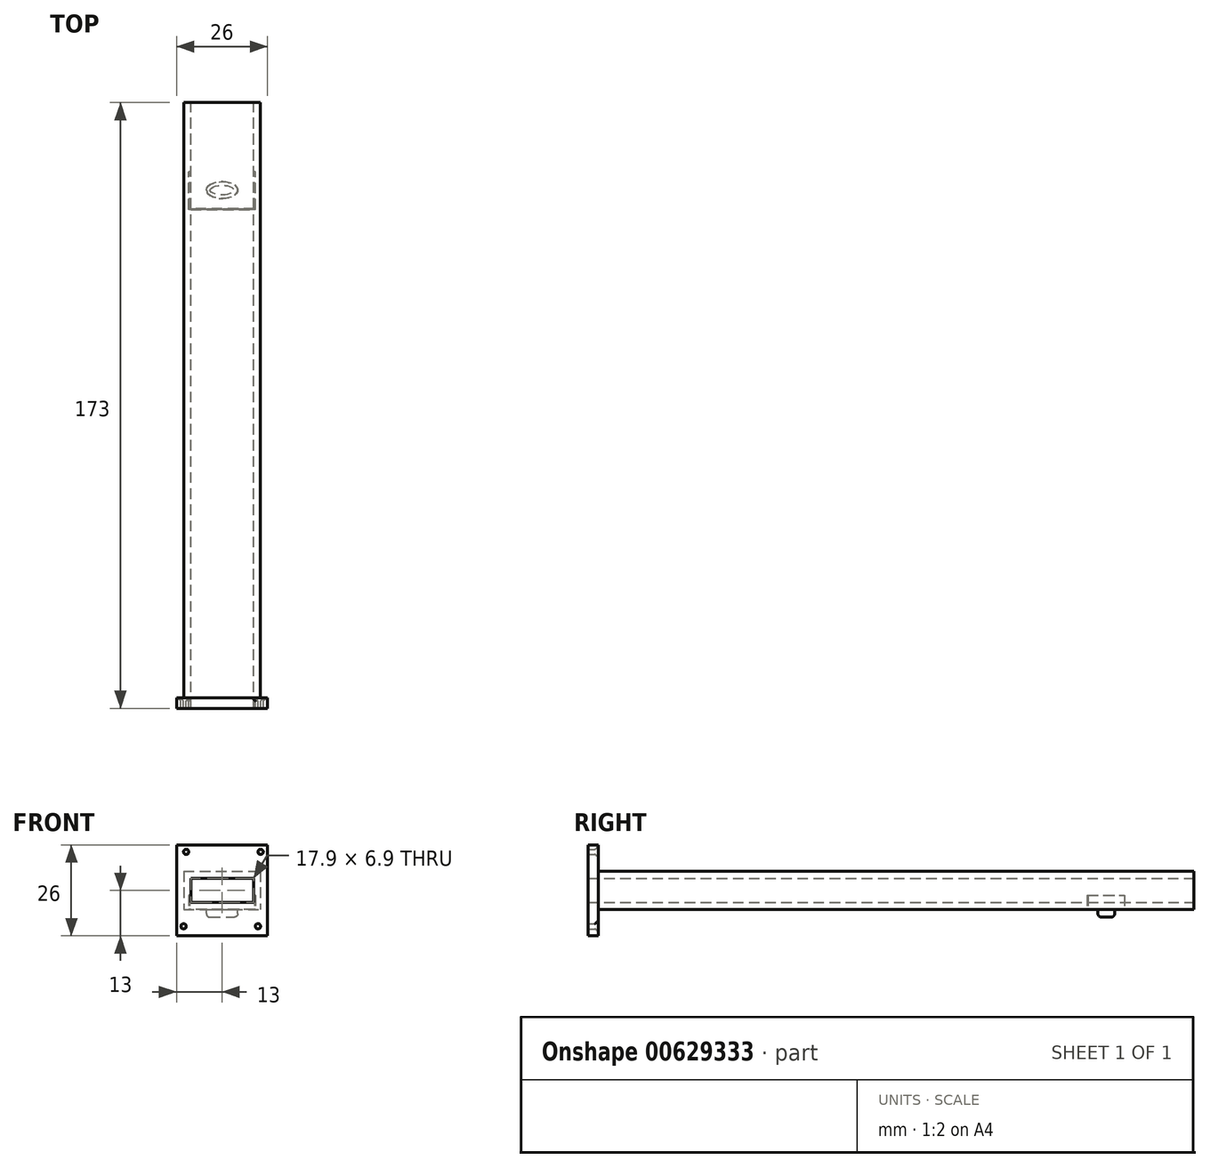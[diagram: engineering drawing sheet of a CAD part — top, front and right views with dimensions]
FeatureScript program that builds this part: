
annotation { "Feature Type Name" : "Feature", "Feature Type Description" : "" }
export const myFeature = defineFeature(function(context is Context, id is Id, definition is map)
    precondition{}
    {
        {
            var Q0;
            Q0=qCreatedBy(makeId("Front.planeOp"),FACE);
            var sketch = newSketch(context, id + "F0", { "sketchPlane" : qUnion([Q0])});
            skLineSegment(sketch, "E0.bottom", {"start": v(-10.95, 5.45) * mm, "end": v(10.95, 5.45) * mm});
            skLineSegment(sketch, "E0.top", {"start": v(-10.95, -5.45) * mm, "end": v(10.95, -5.45) * mm});
            skLineSegment(sketch, "E0.left", {"start": v(-10.95, 5.45) * mm, "end": v(-10.95, -5.45) * mm});
            skLineSegment(sketch, "E0.right", {"start": v(10.95, 5.45) * mm, "end": v(10.95, -5.45) * mm});
            skPoint(sketch, "E0.middle", {"position": v(0, 0) * mm});
            skLineSegment(sketch, "E1.0", {"start": v(8.95, 3.45) * mm, "end": v(8.95, -3.45) * mm});
            skLineSegment(sketch, "E1.1", {"start": v(-8.95, 3.45) * mm, "end": v(8.95, 3.45) * mm});
            skLineSegment(sketch, "E1.2", {"start": v(-8.95, 3.45) * mm, "end": v(-8.95, -3.45) * mm});
            skLineSegment(sketch, "E1.3", {"start": v(-8.95, -3.45) * mm, "end": v(8.95, -3.45) * mm});
            skSolve(sketch);
        }
        {
            var Q0;
            Q0 = qSketchRegion(id + "F0", true);
            extrude(context, id + "F1", {"entities" : qUnion([Q0]), "depth" : 170 * mm, "offsetDistance" : 25 * mm});
        }
        {
            var Q0;
            Q0=makeQuery(id+"F1.opExtrude","SWEPT_FACE",FACE,{"disambiguationData":[OSD([sQuery(id+"F0.wireOp",EDGE,"E0.top")])]});
            var sketch = newSketch(context, id + "F2", { "sketchPlane" : qUnion([Q0])});
            skEllipse(sketch, "E2", {"center": v(0, 25) * mm, "majorRadius": 4.5 * mm, "minorRadius": 2.4 * mm, "majorAxis": v(-1, 0)});
            skLineSegment(sketch, "E3", {"start": v(0, 116.39) * mm, "end": v(0, -29.07) * mm, "construction": true});
            skSolve(sketch);
        }
        {
            var Q0;
            Q0 = qSketchRegion(id + "F2", true);
            extrude(context, id + "F3", {"entities" : qUnion([Q0]), "operationType" : NewBodyOperationType.ADD, "depth" : 2.2 * mm, "offsetDistance" : 25 * mm});
        }
        {
            var Q0;
            Q0=makeQuery(id+"F1.opExtrude","SWEPT_FACE",FACE,{"disambiguationData":[OSD([sQuery(id+"F0.wireOp",EDGE,"E0.top")])]});
            var sketch = newSketch(context, id + "F4", { "sketchPlane" : qUnion([Q0])});
            skPoint(sketch, "E4.0", {"position": v(0, 25) * mm});
            skLineSegment(sketch, "E5.bottom", {"start": v(9.25, 30.25) * mm, "end": v(-9.25, 30.25) * mm});
            skLineSegment(sketch, "E5.left", {"start": v(9.25, 30.25) * mm, "end": v(9.25, 19.75) * mm});
            skLineSegment(sketch, "E5.right", {"start": v(-9.25, 30.25) * mm, "end": v(-9.25, 19.75) * mm});
            skLineSegment(sketch, "E6.0", {"start": v(-9.5, 30.5) * mm, "end": v(-9.5, 19.75) * mm});
            skLineSegment(sketch, "E6.1", {"start": v(9.5, 30.5) * mm, "end": v(-9.5, 30.5) * mm});
            skLineSegment(sketch, "E6.2", {"start": v(9.5, 30.5) * mm, "end": v(9.5, 19.75) * mm});
            skLineSegment(sketch, "E6.3", {"start": v(9.5, 19.75) * mm, "end": v(9.25, 19.75) * mm});
            skLineSegment(sketch, "E7.trimOffspring", {"start": v(-9.25, 19.75) * mm, "end": v(-9.5, 19.75) * mm});
            skSolve(sketch);
        }
        {
            var Q0;
            Q0 = qSketchRegion(id + "F4", true);
            extrude(context, id + "F5", {"entities" : qUnion([Q0]), "operationType" : NewBodyOperationType.REMOVE, "oppositeDirection" : true, "depth" : 4 * mm, "offsetDistance" : 25 * mm});
        }
        {
            var Q0;
            Q0=makeQuery(id+"F1.opExtrude","CAP_FACE",FACE,{"disambiguationData":[OSD([sQuery(id+"F0.wireOp",EDGE,"E0.bottom"),sQuery(id+"F0.wireOp",EDGE,"E0.top"),sQuery(id+"F0.wireOp",EDGE,"E0.left"),sQuery(id+"F0.wireOp",EDGE,"E0.right"),sQuery(id+"F0.wireOp",EDGE,"E1.0"),sQuery(id+"F0.wireOp",EDGE,"E1.1"),sQuery(id+"F0.wireOp",EDGE,"E1.2"),sQuery(id+"F0.wireOp",EDGE,"E1.3")])],"isStart":false});
            var sketch = newSketch(context, id + "F6", { "sketchPlane" : qUnion([Q0])});
            skLineSegment(sketch, "E8.bottom", {"start": v(13, 13) * mm, "end": v(-13, 13) * mm});
            skLineSegment(sketch, "E8.top", {"start": v(13, -13) * mm, "end": v(-13, -13) * mm});
            skLineSegment(sketch, "E8.left", {"start": v(13, 13) * mm, "end": v(13, -13) * mm});
            skLineSegment(sketch, "E8.right", {"start": v(-13, 13) * mm, "end": v(-13, -13) * mm});
            skPoint(sketch, "E8.middle", {"position": v(0, 0) * mm});
            skLineSegment(sketch, "E9", {"start": v(8.95, 3.45) * mm, "end": v(8.95, -3.45) * mm});
            skLineSegment(sketch, "E10", {"start": v(8.95, -3.45) * mm, "end": v(-8.95, -3.45) * mm});
            skLineSegment(sketch, "E11", {"start": v(-8.95, -3.45) * mm, "end": v(-8.95, 3.45) * mm});
            skLineSegment(sketch, "E12", {"start": v(-8.95, 3.45) * mm, "end": v(8.95, 3.45) * mm});
            skCircle(sketch, "E13", {"center": v(11, 11) * mm, "radius": 0.75 * mm});
            skCircle(sketch, "E14", {"center": v(-10.25, 11) * mm, "radius": 0.75 * mm});
            skCircle(sketch, "E15", {"center": v(-11, -10.25) * mm, "radius": 0.75 * mm});
            skCircle(sketch, "E16", {"center": v(10.25, -10.25) * mm, "radius": 0.75 * mm});
            skSolve(sketch);
        }
        {
            var Q0;
            Q0=makeQuery(id+"F6.imprint","IMPRINT",FACE,{"disambiguationData":[TD([[makeQuery(id+"F6.imprint","IMPRINT",EDGE,{"derivedFrom":sQuery(id+"F6.wireOp",EDGE,"E8.bottom")}),1.0]])]});
            var Q1;
            Q1=makeQuery(id+"F6.imprint","IMPRINT",FACE,{"disambiguationData":[TD([[makeQuery(id+"F6.imprint","IMPRINT",EDGE,{"derivedFrom":sQuery(id+"F6.wireOp",EDGE,"E9")}),1.0]])]});
            var Q2;
            Q2 = qBodyType(qCreatedBy(id + "F6" ,EDGE), BodyType.WIRE);
            extrude(context, id + "F7", {"entities" : qUnion([Q0, Q1]), "operationType" : NewBodyOperationType.ADD, "surfaceEntities" : qUnion([Q2]), "depth" : 3 * mm, "offsetDistance" : 25 * mm});
        }
        {
            var Q0;
            Q0=makeQuery(id+"F7.opExtrude","CAP_EDGE",EDGE,{"disambiguationData":[OSD([sQuery(id+"F6.wireOp",EDGE,"E13")])],"isStart":true});
            var Q1;
            Q1=makeQuery(id+"F7.opExtrude","CAP_EDGE",EDGE,{"disambiguationData":[OSD([sQuery(id+"F6.wireOp",EDGE,"E14")])],"isStart":true});
            var Q2;
            Q2=makeQuery(id+"F7.opExtrude","CAP_EDGE",EDGE,{"disambiguationData":[OSD([sQuery(id+"F6.wireOp",EDGE,"E15")])],"isStart":true});
            var Q3;
            Q3=makeQuery(id+"F7.opExtrude","CAP_EDGE",EDGE,{"disambiguationData":[OSD([sQuery(id+"F6.wireOp",EDGE,"E16")])],"isStart":true});
            fillet(context, id + "F8", {"entities" : qUnion([Q0, Q1, Q2, Q3]), "radius" : 1 * mm, "tangentPropagation" : true, "rho" : 0.1, "crossSection" : FilletCrossSection.CONIC, "allowEdgeOverflow" : false});
        }
        {
            var Q0;
            Q0=makeQuery(id+"F3.opExtrude","CAP_EDGE",EDGE,{"disambiguationData":[OSD([sQuery(id+"F2.wireOp",EDGE,"E2")])],"isStart":false});
            fillet(context, id + "F9", {"entities" : qUnion([Q0]), "radius" : 1 * mm, "tangentPropagation" : true, "allowEdgeOverflow" : false});
        }
    });
